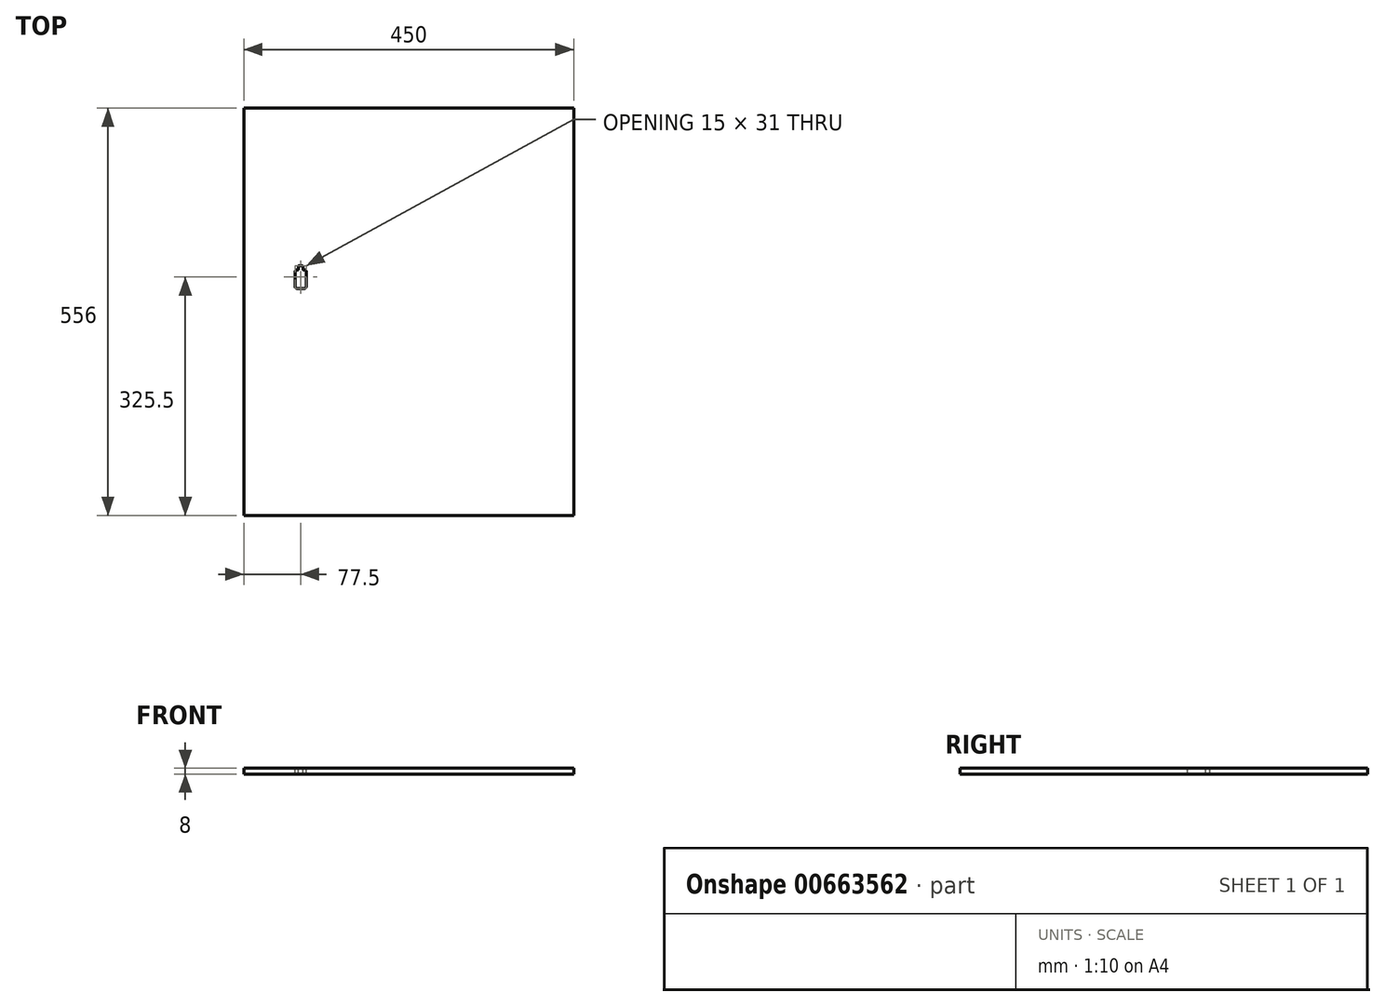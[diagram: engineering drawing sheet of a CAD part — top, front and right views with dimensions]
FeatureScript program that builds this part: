
annotation { "Feature Type Name" : "Feature", "Feature Type Description" : "" }
export const myFeature = defineFeature(function(context is Context, id is Id, definition is map)
    precondition{}
    {
        {
            var Q0;
            Q0=qCreatedBy(makeId("Top.planeOp"),FACE);
            var sketch = newSketch(context, id + "F0", { "sketchPlane" : qUnion([Q0])});
            skLineSegment(sketch, "E0.bottom", {"start": v(-225, 278) * mm, "end": v(225, 278) * mm});
            skLineSegment(sketch, "E0.top", {"start": v(-225, -278) * mm, "end": v(225, -278) * mm});
            skLineSegment(sketch, "E0.left", {"start": v(-225, 278) * mm, "end": v(-225, -278) * mm});
            skLineSegment(sketch, "E0.right", {"start": v(225, 278) * mm, "end": v(225, -278) * mm});
            skLineSegment(sketch, "E1", {"start": v(0, 278) * mm, "end": v(0, -278) * mm, "construction": true});
            skLineSegment(sketch, "E2", {"start": v(-225, 0) * mm, "end": v(225, 0) * mm, "construction": true});
            skLineSegment(sketch, "E3.bottom", {"start": v(-155, 57) * mm, "end": v(-150.5, 57) * mm});
            skLineSegment(sketch, "E3.top", {"start": v(-155, 32) * mm, "end": v(-140, 32) * mm});
            skLineSegment(sketch, "E3.left", {"start": v(-155, 57) * mm, "end": v(-155, 32) * mm});
            skLineSegment(sketch, "E3.right", {"start": v(-140, 57) * mm, "end": v(-140, 32) * mm});
            skLineSegment(sketch, "E4", {"start": v(-147.5, 32) * mm, "end": v(-147.5, 95.23) * mm, "construction": true});
            skLineSegment(sketch, "E5", {"start": v(-150.5, 63) * mm, "end": v(-150.5, 57) * mm});
            skLineSegment(sketch, "E6", {"start": v(-144.5, 63) * mm, "end": v(-144.5, 57) * mm});
            skLineSegment(sketch, "E7.trimOffspring", {"start": v(-144.5, 57) * mm, "end": v(-140, 57) * mm});
            skLineSegment(sketch, "E8", {"start": v(-150.5, 63) * mm, "end": v(-144.5, 63) * mm});
            skSolve(sketch);
        }
        {
            var Q0;
            Q0 = qSketchRegion(id + "F0", true);
            extrude(context, id + "F1", {"entities" : qUnion([Q0]), "oppositeDirection" : true, "depth" : 8 * mm, "offsetDistance" : 25 * mm});
        }
        {
            var Q0;
            Q0=makeQuery(id+"F1.opExtrude","SWEPT_EDGE",EDGE,{"disambiguationData":[OSD([sQuery(id+"F0.wireOp",EDGE,"E6"),sQuery(id+"F0.wireOp",EDGE,"E7.trimOffspring")])]});
            var Q1;
            Q1=makeQuery(id+"F1.opExtrude","SWEPT_EDGE",EDGE,{"disambiguationData":[OSD([sQuery(id+"F0.wireOp",EDGE,"E3.bottom"),sQuery(id+"F0.wireOp",EDGE,"E5")])]});
            var Q2;
            Q2=makeQuery(id+"F1.opExtrude","SWEPT_EDGE",EDGE,{"disambiguationData":[OSD([sQuery(id+"F0.wireOp",EDGE,"E6"),sQuery(id+"F0.wireOp",EDGE,"E8")])]});
            var Q3;
            Q3=makeQuery(id+"F1.opExtrude","SWEPT_EDGE",EDGE,{"disambiguationData":[OSD([sQuery(id+"F0.wireOp",EDGE,"E5"),sQuery(id+"F0.wireOp",EDGE,"E8")])]});
            fillet(context, id + "F2", {"entities" : qUnion([Q0, Q1, Q2, Q3]), "radius" : 1 * mm, "tangentPropagation" : true, "allowEdgeOverflow" : false});
        }
        {
            var Q0;
            Q0=makeQuery(id+"F1.opExtrude","SWEPT_EDGE",EDGE,{"disambiguationData":[OSD([sQuery(id+"F0.wireOp",EDGE,"E3.right"),sQuery(id+"F0.wireOp",EDGE,"E7.trimOffspring")])]});
            var Q1;
            Q1=makeQuery(id+"F1.opExtrude","SWEPT_EDGE",EDGE,{"disambiguationData":[OSD([sQuery(id+"F0.wireOp",EDGE,"E3.top"),sQuery(id+"F0.wireOp",EDGE,"E3.right")])]});
            var Q2;
            Q2=makeQuery(id+"F1.opExtrude","SWEPT_EDGE",EDGE,{"disambiguationData":[OSD([sQuery(id+"F0.wireOp",EDGE,"E3.bottom"),sQuery(id+"F0.wireOp",EDGE,"E3.left")])]});
            var Q3;
            Q3=makeQuery(id+"F1.opExtrude","SWEPT_EDGE",EDGE,{"disambiguationData":[OSD([sQuery(id+"F0.wireOp",EDGE,"E3.top"),sQuery(id+"F0.wireOp",EDGE,"E3.left")])]});
            fillet(context, id + "F3", {"entities" : qUnion([Q0, Q1, Q2, Q3]), "radius" : 2 * mm, "tangentPropagation" : true, "allowEdgeOverflow" : false});
        }
    });
